FCSTD DOCUMENT  (FreeCAD 0.19R0.19.2)
Label: v0_07_mount positionLinesInPlace
License: All rights reserved
LicenseURL: http://en.wikipedia.org/wiki/All_rights_reserved
objects: Sketcher::SketchObject×1
note: 1 computed .brp shape members not serialized (recipe doc carries the construction recipe); baked Part::Feature solids carry a one-line shape summary decoded from their .brp

FEATURE [Sketcher::SketchObject] Sketch
  FullyConstrained = false
  sketch-geometry (53):
    g0: LineSegment StartX=0 StartY=0 StartZ=0 EndX=111.35 EndY=0 EndZ=0
    g1: Circle CenterX=111.35 CenterY=-15.15 CenterZ=0 NormalX=0 NormalY=0 NormalZ=1 AngleXU=0 Radius=3.25
    g2: LineSegment StartX=111.35 StartY=0 StartZ=0 EndX=144.4 EndY=0 EndZ=0
    g3: LineSegment StartX=144.9 StartY=-7.5 StartZ=0 EndX=151.9 EndY=-7.5 EndZ=0
    g4: LineSegment StartX=111.35 StartY=0 StartZ=0 EndX=98.1 EndY=0 EndZ=0
    g5: Circle CenterX=106.25 CenterY=37.0888 CenterZ=0 NormalX=0 NormalY=0 NormalZ=1 AngleXU=0 Radius=1.3
    g6: Circle CenterX=86.1497 CenterY=37.0888 CenterZ=0 NormalX=0 NormalY=0 NormalZ=1 AngleXU=0 Radius=1.3
    g7: LineSegment StartX=111.35 StartY=0 StartZ=0 EndX=81.35 EndY=0 EndZ=0
    g8: LineSegment StartX=144.4 StartY=0 StartZ=0 EndX=144.4 EndY=-7 EndZ=0
    g9: ArcOfCircle CenterX=144.9 CenterY=-7 CenterZ=0 NormalX=0 NormalY=0 NormalZ=1 AngleXU=0 Radius=0.5 StartAngle=3.14159 EndAngle=4.71239
    g10: Circle CenterX=106.25 CenterY=29.0888 CenterZ=0 NormalX=0 NormalY=0 NormalZ=1 AngleXU=0 Radius=1.3
    g11: Circle CenterX=86.1497 CenterY=29.0888 CenterZ=0 NormalX=0 NormalY=0 NormalZ=1 AngleXU=0 Radius=1.3
    g12: LineSegment StartX=151.9 StartY=-7.5 StartZ=0 EndX=151.9 EndY=-20.4 EndZ=0
    g13: LineSegment StartX=86.1497 StartY=29.0888 StartZ=0 EndX=106.25 EndY=29.0888 EndZ=0
    g14: LineSegment StartX=106.25 StartY=29.0888 StartZ=0 EndX=106.25 EndY=37.0888 EndZ=0
    g15: LineSegment StartX=86.1497 StartY=29.0888 StartZ=0 EndX=86.1497 EndY=37.0888 EndZ=0
    g16: LineSegment StartX=81.35 StartY=0 StartZ=0 EndX=81.35 EndY=-35.3 EndZ=0
    g17: LineSegment StartX=44.35 StartY=-35.3 StartZ=0 EndX=81.35 EndY=-35.3 EndZ=0
    g18: LineSegment StartX=81.35 StartY=-35.3 StartZ=0 EndX=151.9 EndY=-35.3 EndZ=0
    g19: LineSegment StartX=151.9 StartY=-20.4 StartZ=0 EndX=151.9 EndY=-35.3 EndZ=0
    g20: LineSegment StartX=44.35 StartY=2.2e-15 StartZ=0 EndX=44.35 EndY=-28 EndZ=0
    g21-g25: Circle x5 (B-spline internal-alignment scaffolding for g26; pole/knot coordinates omitted)
    g26: BSplineCurve PolesCount=5 KnotsCount=3 Degree=3 IsPeriodic=0
    g27: GeomPoint X=15.15 Y=-28 Z=0
    g28: GeomPoint X=29.75 Y=-31.65 Z=0
    g29: GeomPoint X=44.35 Y=-35.3 Z=0
    g30: LineSegment StartX=0 StartY=0 StartZ=0 EndX=0 EndY=-28 EndZ=0
    g31: LineSegment StartX=15.15 StartY=-28 StartZ=0 EndX=0 EndY=-28 EndZ=0
    g32: LineSegment StartX=-10 StartY=0 StartZ=0 EndX=0 EndY=0 EndZ=0
    g33: ArcOfCircle CenterX=-15 CenterY=-9 CenterZ=0 NormalX=0 NormalY=0 NormalZ=1 AngleXU=0 Radius=2.5 StartAngle=1.5708 EndAngle=3.14159
    g34: LineSegment StartX=-17.5 StartY=-9 StartZ=0 EndX=-17.5 EndY=-11.5 EndZ=0
    g35: LineSegment StartX=-12.5 StartY=-12.75 StartZ=0 EndX=-10 EndY=-12.75 EndZ=0
    g36: LineSegment StartX=-12.5 StartY=-14 StartZ=0 EndX=-12.5 EndY=-12.75 EndZ=0
    g37: LineSegment StartX=-12.5 StartY=-21.5 StartZ=0 EndX=-10 EndY=-21.5 EndZ=0
    g38: LineSegment StartX=-12.5 StartY=-28 StartZ=0 EndX=0 EndY=-28 EndZ=0
    g39: ArcOfCircle CenterX=-10 CenterY=-15.25 CenterZ=0 NormalX=0 NormalY=0 NormalZ=1 AngleXU=0 Radius=2.5 StartAngle=0 EndAngle=1.5708
    g40: LineSegment StartX=-7.5 StartY=-15.25 StartZ=0 EndX=-7.5 EndY=-19 EndZ=0
    g41: ArcOfCircle CenterX=-10 CenterY=-19 CenterZ=0 NormalX=0 NormalY=0 NormalZ=1 AngleXU=0 Radius=2.5 StartAngle=4.71239 EndAngle=6.28319
    g42: LineSegment StartX=-12.5 StartY=-14 StartZ=0 EndX=-12.5 EndY=-15.25 EndZ=0
    g43: LineSegment StartX=-17.5 StartY=-11.5 StartZ=0 EndX=-17.5 EndY=-12.75 EndZ=0
    g44: LineSegment StartX=-15 StartY=-15.25 StartZ=0 EndX=-12.5 EndY=-15.25 EndZ=0
    g45: ArcOfCircle CenterX=-15 CenterY=-12.75 CenterZ=0 NormalX=0 NormalY=0 NormalZ=1 AngleXU=0 Radius=2.5 StartAngle=3.14159 EndAngle=4.71239
    g46: LineSegment StartX=-10 StartY=0 StartZ=0 EndX=-10 EndY=-4 EndZ=0
    g47: LineSegment StartX=-15 StartY=-4 StartZ=0 EndX=-10 EndY=-4 EndZ=0
    g48: LineSegment StartX=-15 StartY=-4 StartZ=0 EndX=-15 EndY=-6.5 EndZ=0
    g49: LineSegment StartX=-17.5 StartY=-28 StartZ=0 EndX=-12.5 EndY=-28 EndZ=0
    g50: LineSegment StartX=-17.5 StartY=-24 StartZ=0 EndX=-17.5 EndY=-28 EndZ=0
    g51: LineSegment StartX=-17.5 StartY=-24 StartZ=0 EndX=-12.5 EndY=-24 EndZ=0
    g52: LineSegment StartX=-12.5 StartY=-21.5 StartZ=0 EndX=-12.5 EndY=-24 EndZ=0
  constraints (117):
    c: Coincident(g0,g-1)
    c: PointOnObject(g0,g-1)
    c: Distance(g0) = 111.35
    c: Radius(g1) = 3.25
    c: Block(g1)
    c: Horizontal(g2)
    c: Distance(g2) = 33.05
    c: Coincident(g2,g0)
    c: Horizontal(g4)
    c: Distance(g4) = 13.25
    c: Coincident(g4,g0)
    c: Horizontal(g7)
    c: Distance(g7) = 30
    c: Coincident(g7,g0)
    c: Vertical(g8)
    c: Distance(g8) = 7
    c: Coincident(g8,g2)
    c: Coincident(g9,g8)
    c: Coincident(g9,g3)
    c: Block(g3)
    c: Block(g9)
    c: Vertical(g12)
    c: Coincident(g12,g3)
    c: Block(g12)
    c: Horizontal(g13)
    c: Vertical(g14)
    c: Vertical(g15)
    c: Coincident(g15,g6)
    c: Coincident(g15,g11)
    c: Coincident(g13,g11)
    c: Coincident(g13,g10)
    c: Coincident(g14,g10)
    c: Coincident(g5,g14)
    c: DistanceX(g13,g13) = 20.1
    c: DistanceY(g15,g15) = 8
    c: DistanceY(g14,g14) = 8
    c: Vertical(g16)
    c: Distance(g16) = 35.3
    c: Coincident(g16,g7)
    c: Horizontal(g17)
    c: Distance(g17) = 37
    c: Coincident(g17,g16)
    c: Horizontal(g18)
    c: Coincident(g18,g16)
    c: Vertical(g19)
    c: Coincident(g18,g19)
    c: Vertical(g20)
    c: Distance(g20) = 28
    c: Block(g20)
    c: Weight(g21) = 1
    c: Equal(g21, g22-g25) x4
    c: Coincident(g26,g17)
    c: InternalAlignment(g21-g25 -> g26) x5
    c: InternalAlignment(g27,g26)
    c: InternalAlignment(g28,g26)
    c: InternalAlignment(g29,g26)
    c: Vertical(g30)
    c: Coincident(g30,g0)
    c: Horizontal(g31)
    c: Coincident(g31,g30)
    c: Block(g26)
    c: Block(g18)
    c: Block(g19)
    c: Block(g31)
    c: Horizontal(g32)
    c: Distance(g32) = 10
    c: Coincident(g32,g0)
    c: Vertical(g34)
    c: Block(g34)
    c: Block(g33)
    c: Distance(g35) = 2.5
    c: Horizontal(g35)
    c: Vertical(g36)
    c: Distance(g36) = 1.25
    c: Coincident(g35,g36)
    c: Horizontal(g37)
    c: Distance(g37) = 2.5
    c: Horizontal(g38)
    c: Coincident(g38,g30)
    c: Coincident(g39,g35)
    c: Vertical(g40)
    c: Block(g39)
    c: Block(g40)
    c: Block(g41)
    c: Block(g38)
    c: Vertical(g42)
    c: Distance(g42) = 1.25
    c: Vertical(g43)
    c: Distance(g43) = 1.25
    c: Coincident(g43,g34)
    c: Horizontal(g44)
    c: Distance(g44) = 2.5
    c: Coincident(g44,g42)
    c: Coincident(g45,g44)
    c: Coincident(g45,g43)
    c: Block(g45)
    c: Vertical(g46)
    c: Distance(g46) = 4
    c: Coincident(g46,g32)
    c: Horizontal(g47)
    c: Coincident(g47,g46)
    c: Vertical(g48)
    c: Coincident(g48,g33)
    c: Coincident(g48,g47)
    c: Horizontal(g49)
    c: Distance(g49) = 5
    c: Vertical(g50)
    c: Distance(g50) = 4
    c: Coincident(g50,g49)
    c: Horizontal(g51)
    c: Block(g49)
    c: Coincident(g51,g50)
    c: Vertical(g52)
    c: Coincident(g52,g37)
    c: Coincident(g51,g52)
    c: Block(g51)
    c: Block(g37)
